FCSTD DOCUMENT  (FreeCAD 0.18R16146 (Git))
Label: laundry sink hangers
License: All rights reserved
LicenseURL: http://en.wikipedia.org/wiki/All_rights_reserved
objects: Sketcher::SketchObject×1, PartDesign::Body×1
note: 2 computed .brp shape members not serialized (recipe doc carries the construction recipe); baked Part::Feature solids carry a one-line shape summary decoded from their .brp

FEATURE [Sketcher::SketchObject] Sketch
  MapMode = 5
  Support = -> [XY_Plane]
  sketch-geometry (12):
    g0: LineSegment StartX=0 StartY=0 StartZ=0 EndX=0 EndY=5 EndZ=0
    g1: LineSegment StartX=0 StartY=5 StartZ=0 EndX=7 EndY=5 EndZ=0
    g2: LineSegment StartX=7 StartY=5 StartZ=0 EndX=8 EndY=-1.59734 EndZ=0
    g3: LineSegment StartX=8 StartY=-1.59734 StartZ=0 EndX=10.5174 EndY=-1 EndZ=0
    g4: LineSegment StartX=10.5174 StartY=-1 StartZ=0 EndX=9 EndY=5.31162 EndZ=0
    g5: LineSegment StartX=9 StartY=5.31162 StartZ=0 EndX=8.28497 EndY=5 EndZ=0
    g6: LineSegment StartX=8.28497 StartY=5 StartZ=0 EndX=9.47817 EndY=-0.404145 EndZ=0
    g7: LineSegment StartX=9.47817 StartY=-0.404145 StartZ=0 EndX=8.43894 EndY=-0.692821 EndZ=0
    g8: LineSegment StartX=8.43894 StartY=-0.692821 StartZ=0 EndX=7.34197 EndY=6 EndZ=0
    g9: LineSegment StartX=7.34197 StartY=6 StartZ=0 EndX=-1 EndY=6 EndZ=0
    g10: LineSegment StartX=-1 StartY=6 StartZ=0 EndX=-1 EndY=0 EndZ=0
    g11: LineSegment StartX=-1 StartY=0 StartZ=0 EndX=0 EndY=0 EndZ=0
  constraints (18):
    c: Coincident(g-1,g0)
    c: Vertical(g0)
    c: Coincident(g0,g1)
    c: Horizontal(g1)
    c: Coincident(g1,g2)
    c: Coincident(g2,g3)
    c: Coincident(g3,g4)
    c: Coincident(g4,g5)
    c: Coincident(g5,g6)
    c: Coincident(g6,g7)
    c: Coincident(g7,g8)
    c: Coincident(g8,g9)
    c: Horizontal(g9)
    c: Coincident(g9,g10)
    c: PointOnObject(g10,g-1)
    c: Vertical(g10)
    c: Coincident(g10,g11)
    c: Coincident(g11,g0)
FEATURE [PartDesign::Body] Body
  Group = -> [Sketch]
  Origin = -> Origin
